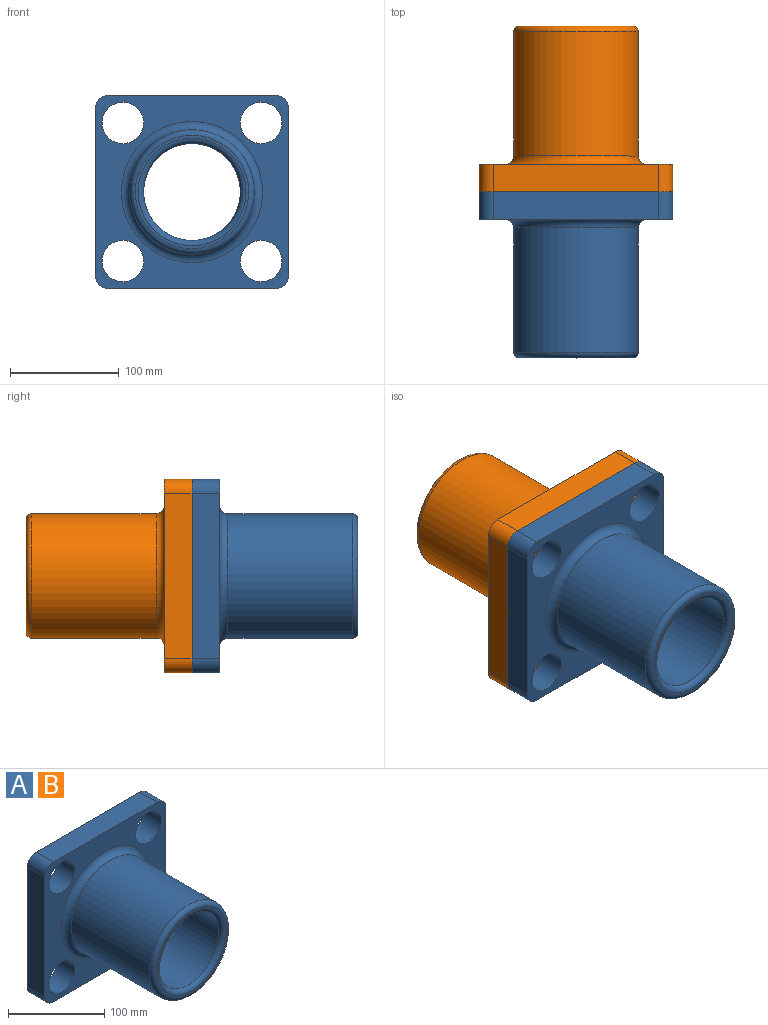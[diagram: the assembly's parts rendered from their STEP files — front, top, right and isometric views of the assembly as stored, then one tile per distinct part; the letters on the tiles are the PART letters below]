
ASSEMBLY  parts=2 mates=1
PART A: 20 faces, bbox 177.8x152.4x177.8 mm
  f0: plane 152.4x25.4mm, normal (0,0,1), area 3871mm2, adj f4,f5,f10,f13
  f1: plane 152.4x25.4mm, normal (-1,0,0), area 3871mm2, adj f4,f5,f10,f11
  f2: plane 152.4x25.4mm, normal (0,0,-1), area 3871mm2, adj f4,f5,f11,f12
  f3: plane 152.4x25.4mm, normal (1,0,0), area 3871mm2, adj f4,f5,f12,f13
  f4: plane 177.8x177.8mm, normal (0,-1,0), area 13734.6mm2, adj f0,f1,f2,f3,f6,f7,f8,f9
  f5: plane 177.8x177.8mm, normal (0,1,0), area 20706.9mm2, adj f0,f1,f2,f3,f6,f7,f8,f9
  f6: cylinder r=19.05mm len=38.1mm, axis (0,-1,0), area 3040.2mm2, adj f4,f5
  f7: cylinder r=19.05mm len=38.1mm, axis (0,-1,0), area 3040.2mm2, adj f4,f5
  f8: cylinder r=19.05mm len=38.1mm, axis (0,-1,0), area 3040.2mm2, adj f4,f5
  f9: cylinder r=19.05mm len=38.1mm, axis (0,-1,0), area 3040.2mm2, adj f4,f5
  f10: cylinder r=12.7mm len=25.4mm, axis (0,-1,0), area 506.7mm2, adj f0,f1,f4,f5
  f11: cylinder r=12.7mm len=25.4mm, axis (0,1,0), area 506.7mm2, adj f1,f2,f4,f5
  f12: cylinder r=12.7mm len=25.4mm, axis (0,-1,0), area 506.7mm2, adj f2,f3,f4,f5
  f13: cylinder r=12.7mm len=25.4mm, axis (0,1,0), area 506.7mm2, adj f0,f3,f4,f5
  f14: cylinder r=44.45mm len=147.32mm, axis (0,1,0), area 41144.6mm2, adj f5,f18
  f15: cylinder r=57.15mm len=114.3mm, axis (0,1,0), area 41043.3mm2, adj f17,f19
  f16: plane 104.14x104.14mm, normal (0,-1,0), area 810.7mm2, adj f18,f19
  f17: torus R=64.77mm, axis (0,-1,0), area 4506.3mm2, adj f4,f15
  f18: torus R=49.53mm, axis (0,-1,0), area 2321.2mm2, adj f14,f16
  f19: torus R=52.07mm, axis (0,-1,0), area 2772.8mm2, adj f15,f16
PART B: same geometry as A
PLACE A t=(-93.13,-68.11,-37.16)mm
PLACE B rot(axis=(1,0,0),180deg) t=(-93.13,-68.11,-37.16)mm
MATE fastened B.f5 <-> A.f5  axis (0,-1,0) through (-93.13,-68.11,51.74)mm
